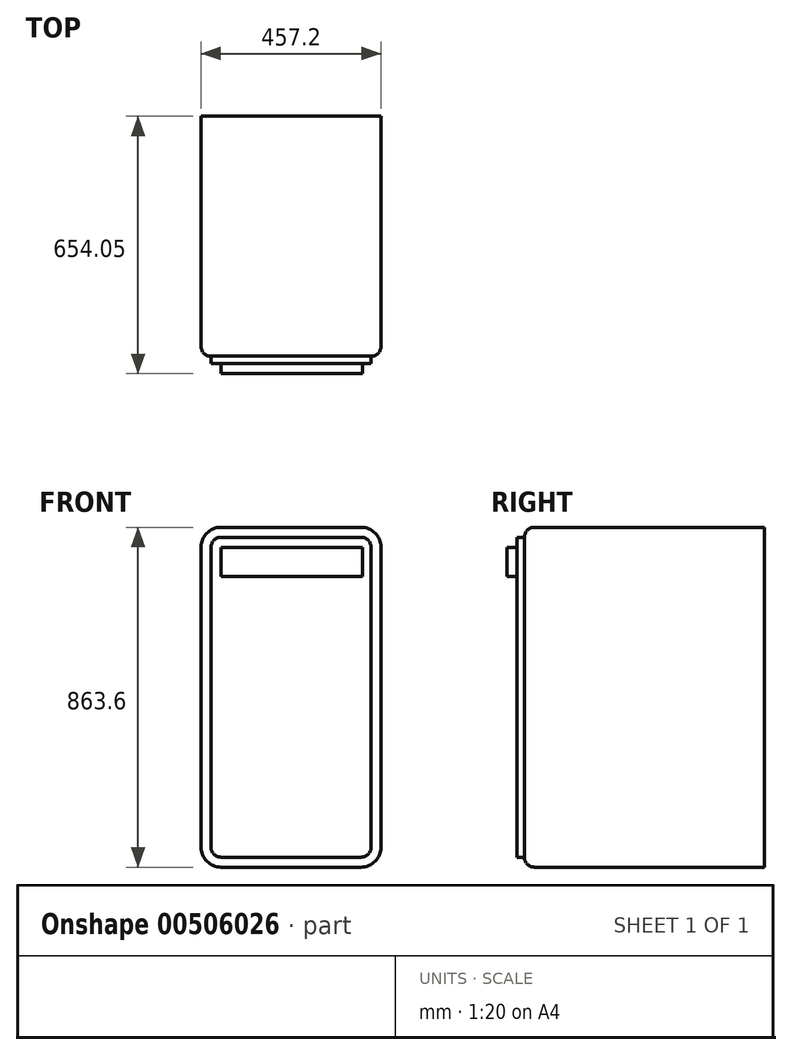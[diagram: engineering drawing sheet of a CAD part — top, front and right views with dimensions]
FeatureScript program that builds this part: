
annotation { "Feature Type Name" : "Feature", "Feature Type Description" : "" }
export const myFeature = defineFeature(function(context is Context, id is Id, definition is map)
    precondition{}
    {
        {
            var Q0;
            Q0=qCreatedBy(makeId("Top.planeOp"),FACE);
            var sketch = newSketch(context, id + "F0", { "sketchPlane" : qUnion([Q0])});
            skLineSegment(sketch, "E0.bottom", {"start": v(0, 0) * mm, "end": v(457.2, 0) * mm});
            skLineSegment(sketch, "E0.top", {"start": v(0, 609.6) * mm, "end": v(457.2, 609.6) * mm});
            skLineSegment(sketch, "E0.left", {"start": v(0, 0) * mm, "end": v(0, 609.6) * mm});
            skLineSegment(sketch, "E0.right", {"start": v(457.2, 0) * mm, "end": v(457.2, 609.6) * mm});
            skSolve(sketch);
        }
        {
            var Q0;
            Q0=makeQuery(id+"F0.imprint","IMPRINT",FACE,{"disambiguationData":[TD([[makeQuery(id+"F0.imprint","IMPRINT",EDGE,{"derivedFrom":sQuery(id+"F0.wireOp",EDGE,"E0.bottom")}),1.0]])]});
            extrude(context, id + "F1", {"entities" : qUnion([Q0]), "depth" : 863.6 * mm, "offsetDistance" : 25.4 * mm});
        }
        {
            var Q0;
            Q0=makeQuery(id+"F1.opExtrude","CAP_EDGE",EDGE,{"disambiguationData":[OSD([sQuery(id+"F0.wireOp",EDGE,"E0.left")])],"isStart":false});
            var Q1;
            Q1=makeQuery(id+"F1.opExtrude","CAP_EDGE",EDGE,{"disambiguationData":[OSD([sQuery(id+"F0.wireOp",EDGE,"E0.right")])],"isStart":false});
            var Q2;
            Q2=makeQuery(id+"F1.opExtrude","CAP_EDGE",EDGE,{"disambiguationData":[OSD([sQuery(id+"F0.wireOp",EDGE,"E0.right")])],"isStart":true});
            var Q3;
            Q3=makeQuery(id+"F1.opExtrude","CAP_EDGE",EDGE,{"disambiguationData":[OSD([sQuery(id+"F0.wireOp",EDGE,"E0.left")])],"isStart":true});
            fillet(context, id + "F2", {"entities" : qUnion([Q0, Q1, Q2, Q3]), "radius" : 50.8 * mm, "tangentPropagation" : true, "allowEdgeOverflow" : false});
        }
        {
            var Q0;
            Q0=makeQuery(id+"F1.opExtrude","CAP_EDGE",EDGE,{"disambiguationData":[OSD([sQuery(id+"F0.wireOp",EDGE,"E0.bottom")])],"isStart":false});
            var Q1;
            Q1=makeQuery(id+"F1.opExtrude","SWEPT_FACE",FACE,{"disambiguationData":[OSD([sQuery(id+"F0.wireOp",EDGE,"E0.bottom")])]});
            fillet(context, id + "F3", {"entities" : qUnion([Q0, Q1]), "radius" : 25.4 * mm, "tangentPropagation" : true, "allowEdgeOverflow" : false});
        }
        {
            var Q0;
            Q0=makeQuery(id+"F1.opExtrude","SWEPT_FACE",FACE,{"disambiguationData":[OSD([sQuery(id+"F0.wireOp",EDGE,"E0.bottom")])]});
            var sketch = newSketch(context, id + "F4", { "sketchPlane" : qUnion([Q0])});
            skSolve(sketch);
        }
        {
            var Q0;
            Q0 = qSketchRegion(id + "F4", true);
            var Q1;
            {var subQ0=sQuery(id+"F0.wireOp",EDGE,"E0.bottom");var subQ1=makeQuery(id+"F1.opExtrude","SWEPT_FACE",FACE,{"disambiguationData":[OSD([subQ0])]});var subQ2=subQ1;Q1=makeQuery(id+"F4.imprint","IMPRINT",FACE,{"disambiguationData":[TD([[makeQuery(id+"F4.imprint","IMPRINT",EDGE,{"derivedFrom":makeQuery(id+"F3.opFillet","BLEND_EDGE",EDGE,{"blendedFrom":[makeQuery(id+"F1.opExtrude","CAP_EDGE",EDGE,{"disambiguationData":[OSD([subQ0])],"isStart":true}),subQ2],"blendedInto":[subQ2]})}),1.0]])]});}
            extrude(context, id + "F5", {"entities" : qUnion([Q0, Q1]), "depth" : 19.05 * mm, "offsetDistance" : 25.4 * mm});
        }
        {
            var Q0;
            Q0=makeQuery(id+"F5.opExtrude","CAP_FACE",FACE,{"disambiguationData":[OSD([sQuery(id+"F0.wireOp",EDGE,"E0.bottom"),sQuery(id+"F0.wireOp",EDGE,"E0.left"),sQuery(id+"F0.wireOp",EDGE,"E0.right")])],"isStart":false});
            var sketch = newSketch(context, id + "F6", { "sketchPlane" : qUnion([Q0])});
            skLineSegment(sketch, "E1.bottom", {"start": v(50.8, 812.8) * mm, "end": v(409.58, 812.8) * mm});
            skLineSegment(sketch, "E1.top", {"start": v(50.8, 738.23) * mm, "end": v(409.58, 738.23) * mm});
            skLineSegment(sketch, "E1.left", {"start": v(50.8, 812.8) * mm, "end": v(50.8, 738.23) * mm});
            skLineSegment(sketch, "E1.right", {"start": v(409.58, 812.8) * mm, "end": v(409.58, 738.23) * mm});
            skSolve(sketch);
        }
        {
            var Q0;
            Q0 = qSketchRegion(id + "F6", true);
            extrude(context, id + "F7", {"entities" : qUnion([Q0]), "depth" : 25.4 * mm, "offsetDistance" : 25.4 * mm});
        }
    });
